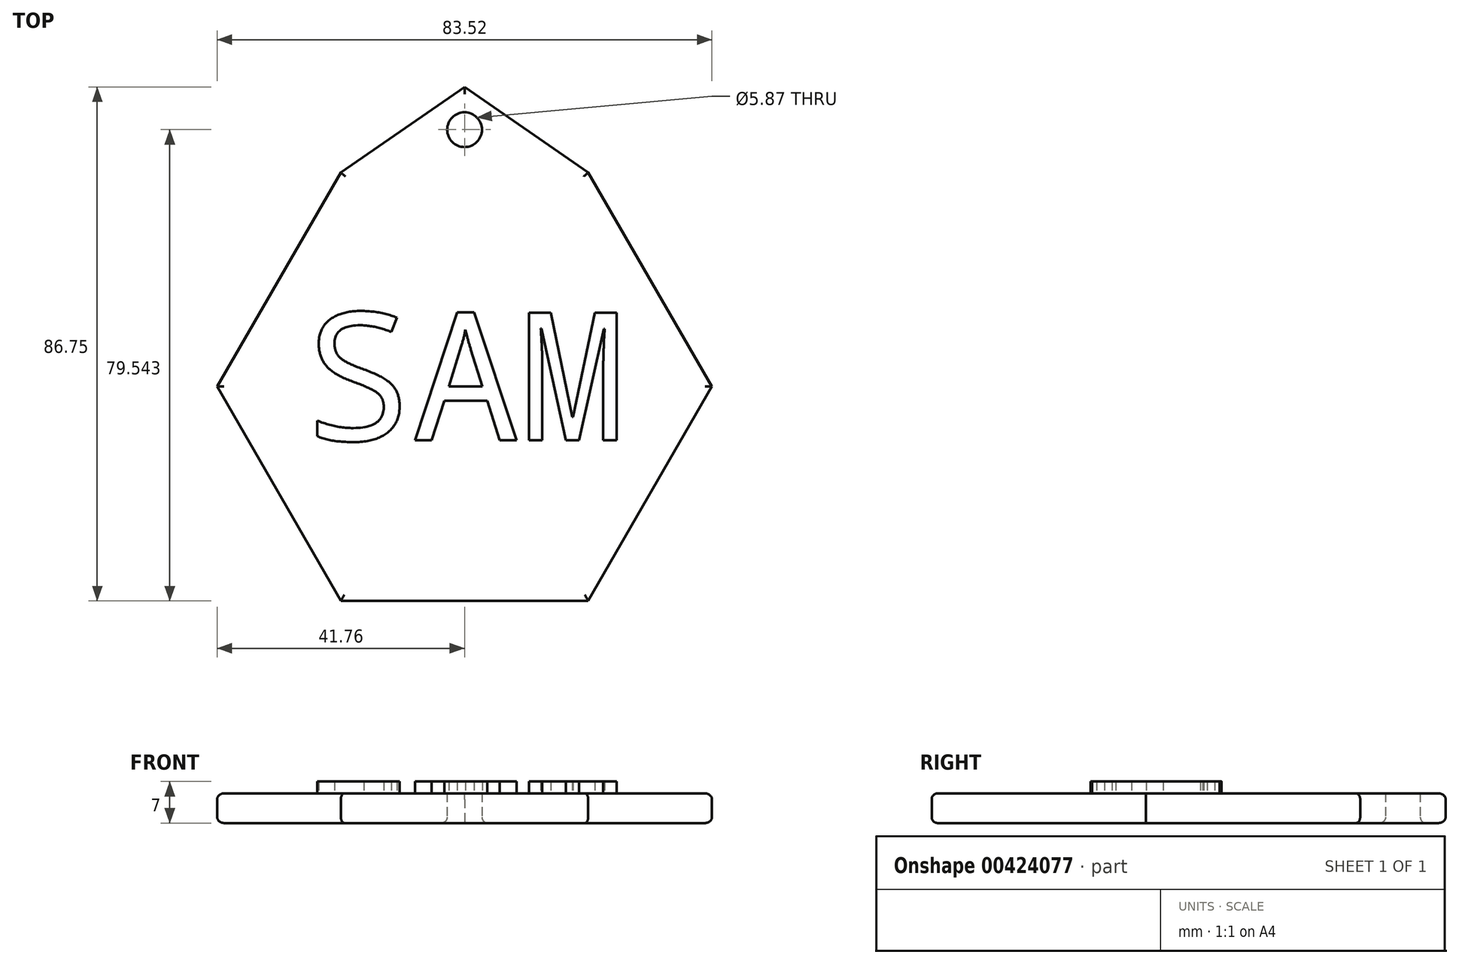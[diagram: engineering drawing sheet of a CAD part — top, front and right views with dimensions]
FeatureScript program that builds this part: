
annotation { "Feature Type Name" : "Feature", "Feature Type Description" : "" }
export const myFeature = defineFeature(function(context is Context, id is Id, definition is map)
    precondition{}
    {
        {
            var Q0;
            Q0=qCreatedBy(makeId("Top.planeOp"),FACE);
            var sketch = newSketch(context, id + "F0", { "sketchPlane" : qUnion([Q0])});
            skCircle(sketch, "E0.cCircle", {"center": v(0, 0) * mm, "radius": 36.17 * mm, "construction": true});
            skLineSegment(sketch, "E0.0", {"start": v(-20.88, 36.17) * mm, "end": v(20.88, 36.17) * mm});
            skLineSegment(sketch, "E0.1", {"start": v(20.88, 36.17) * mm, "end": v(41.76, 0) * mm});
            skLineSegment(sketch, "E0.2", {"start": v(41.76, 0) * mm, "end": v(20.88, -36.17) * mm});
            skLineSegment(sketch, "E0.3", {"start": v(20.88, -36.17) * mm, "end": v(-20.88, -36.17) * mm});
            skLineSegment(sketch, "E0.4", {"start": v(-20.88, -36.17) * mm, "end": v(-41.76, 0) * mm});
            skLineSegment(sketch, "E0.5", {"start": v(-41.76, 0) * mm, "end": v(-20.88, 36.17) * mm});
            skPoint(sketch, "E0.0.midPoint", {"position": v(0, 36.17) * mm});
            skLineSegment(sketch, "E1", {"start": v(-20.88, 36.17) * mm, "end": v(0, 50.58) * mm});
            skLineSegment(sketch, "E2", {"start": v(0, 50.58) * mm, "end": v(20.88, 36.17) * mm});
            skCircle(sketch, "E3", {"center": v(0, 43.37) * mm, "radius": 2.93 * mm});
            skSolve(sketch);
        }
        {
            var Q0;
            Q0 = qSketchRegion(id + "F0", true);
            extrude(context, id + "F1", {"entities" : qUnion([Q0]), "depth" : 5 * mm});
        }
        {
            var Q0;
            Q0=makeQuery(id+"F1.opExtrude","CAP_FACE",FACE,{"disambiguationData":[OSD([sQuery(id+"F0.wireOp",EDGE,"E0.1"),sQuery(id+"F0.wireOp",EDGE,"E0.2"),sQuery(id+"F0.wireOp",EDGE,"E0.3"),sQuery(id+"F0.wireOp",EDGE,"E0.4"),sQuery(id+"F0.wireOp",EDGE,"E0.5"),sQuery(id+"F0.wireOp",EDGE,"E1"),sQuery(id+"F0.wireOp",EDGE,"E2"),sQuery(id+"F0.wireOp",EDGE,"E3")])],"isStart":false});
            var sketch = newSketch(context, id + "F2", { "sketchPlane" : qUnion([Q0])});
            skText(sketch, "E4", { "text": "SAM", "fontName": "DroidSansMono.ttf"});
            const initialGuessF2  = {"E4": [-0.02697, -0.00907, 1, 0, 0.02172]};
            skSetInitialGuess(sketch, initialGuessF2);
            skSolve(sketch);
        }
        {
            var Q0;
            Q0 = qSketchRegion(id + "F2", true);
            extrude(context, id + "F3", {"entities" : qUnion([Q0]), "operationType" : NewBodyOperationType.ADD, "depth" : 2 * mm});
        }
        {
            var Q0;
            Q0=makeQuery(id+"F1.opExtrude","CAP_EDGE",EDGE,{"disambiguationData":[OSD([sQuery(id+"F0.wireOp",EDGE,"E2")])],"isStart":false});
            var Q1;
            Q1=makeQuery(id+"F1.opExtrude","CAP_EDGE",EDGE,{"disambiguationData":[OSD([sQuery(id+"F0.wireOp",EDGE,"E0.1")])],"isStart":false});
            var Q2;
            Q2=makeQuery(id+"F1.opExtrude","CAP_EDGE",EDGE,{"disambiguationData":[OSD([sQuery(id+"F0.wireOp",EDGE,"E0.2")])],"isStart":false});
            var Q3;
            Q3=makeQuery(id+"F1.opExtrude","CAP_EDGE",EDGE,{"disambiguationData":[OSD([sQuery(id+"F0.wireOp",EDGE,"E0.3")])],"isStart":false});
            var Q4;
            Q4=makeQuery(id+"F1.opExtrude","CAP_EDGE",EDGE,{"disambiguationData":[OSD([sQuery(id+"F0.wireOp",EDGE,"E0.4")])],"isStart":false});
            var Q5;
            Q5=makeQuery(id+"F1.opExtrude","CAP_EDGE",EDGE,{"disambiguationData":[OSD([sQuery(id+"F0.wireOp",EDGE,"E1")])],"isStart":false});
            var Q6;
            Q6=makeQuery(id+"F1.opExtrude","CAP_EDGE",EDGE,{"disambiguationData":[OSD([sQuery(id+"F0.wireOp",EDGE,"E0.5")])],"isStart":false});
            var Q7;
            Q7=makeQuery(id+"F1.opExtrude","CAP_FACE",FACE,{"disambiguationData":[OSD([sQuery(id+"F0.wireOp",EDGE,"E0.1"),sQuery(id+"F0.wireOp",EDGE,"E0.2"),sQuery(id+"F0.wireOp",EDGE,"E0.3"),sQuery(id+"F0.wireOp",EDGE,"E0.4"),sQuery(id+"F0.wireOp",EDGE,"E0.5"),sQuery(id+"F0.wireOp",EDGE,"E1"),sQuery(id+"F0.wireOp",EDGE,"E2"),sQuery(id+"F0.wireOp",EDGE,"E3")])],"isStart":true});
            fillet(context, id + "F4", {"entities" : qUnion([Q0, Q1, Q2, Q3, Q4, Q5, Q6, Q7]), "radius" : 1 * mm, "tangentPropagation" : true, "allowEdgeOverflow" : false});
        }
    });
